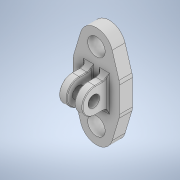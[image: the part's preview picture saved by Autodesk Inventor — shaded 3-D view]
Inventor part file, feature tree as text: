
AUTODESK INVENTOR PART (.ipt)
format: ipt  version: 2021.3 (Build 253353010, 353A)  size: 266,752 bytes
history: native  units: mm
features: extrude x3, fillet x3, sketch x3
ambient origin geometry x8: Origin, YZ Plane, XZ Plane, XY Plane, X Axis, Y Axis, Z Axis, Center Point
bodies: Volumenkörper1 (feature_tree)
feature tree (9):
  extrude  "Extrusion1"  Depth=9.9mm
  extrude  "Extrusion2"  Depth=10.0mm TaperAngle=0.0deg
  extrude  "Extrusion3"  Depth=0.5mm
  fillet  "Rundung1"  Radius=10.0mm
  fillet  "Rundung2"  Radius=3.0mm
  fillet  "Rundung3"  Radius=6.8mm
  sketch  "Skizze1"  dims[d0=3.0mm d1=9.9mm]
  sketch  "Skizze2"  dims[d2=3.07mm d3=10.0mm d4=0.0mm]
  sketch  "Skizze3"  dims[d5=4.5mm d7=0.5mm d8=10.0mm d9=0.0mm d12=3.0mm d13=6.8mm d15=18.0mm d16=5.0mm d17=0.0mm d19=5.0mm d21=5.0mm d32=0.5mm d33=2.0mm d34=0.25mm]
